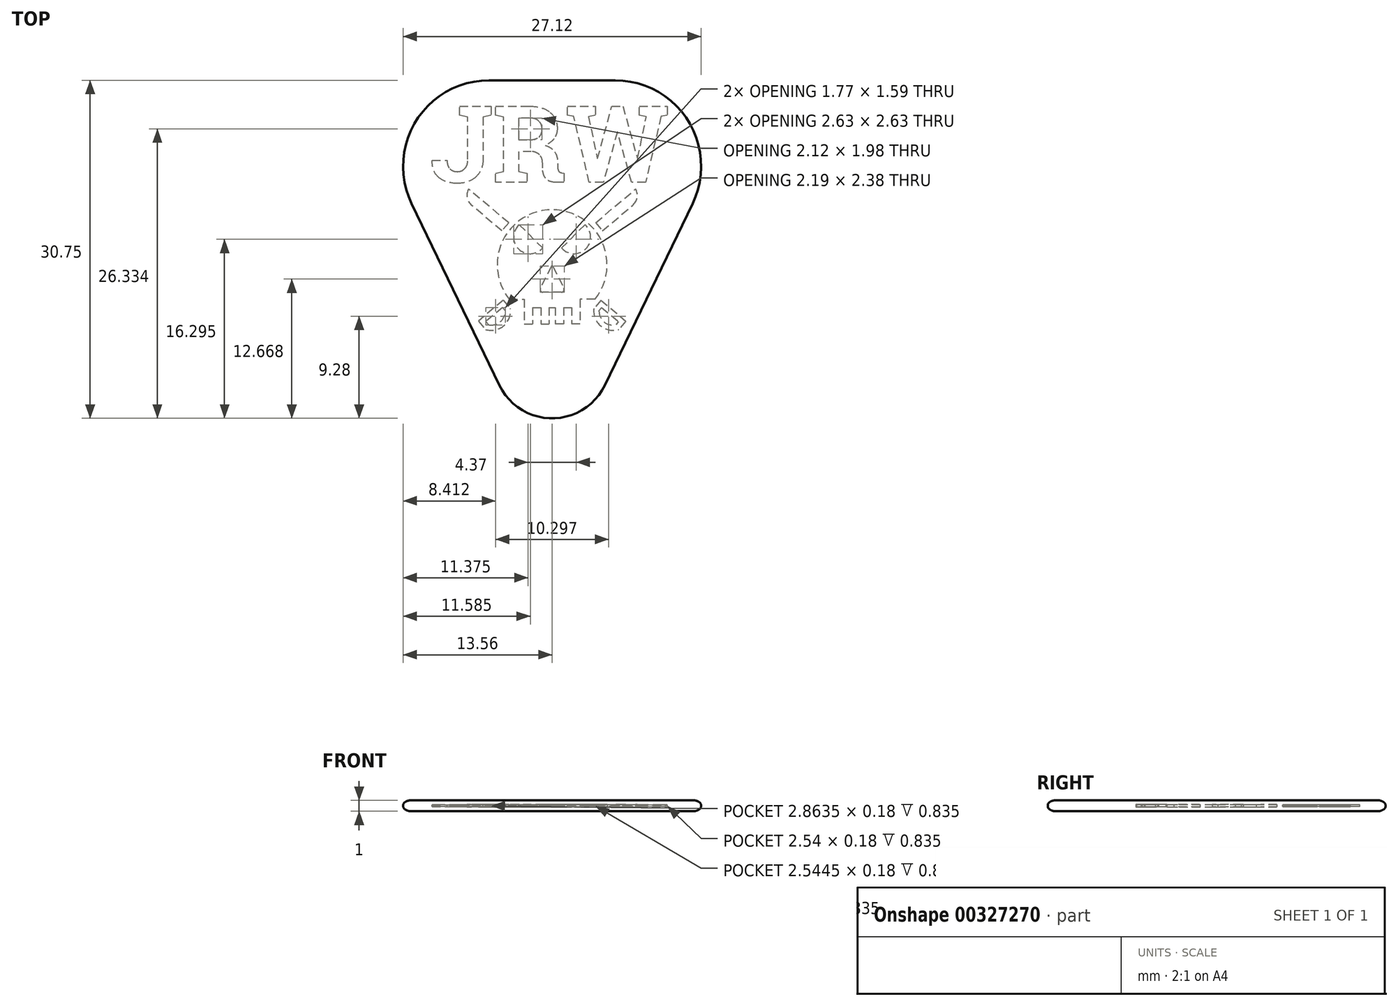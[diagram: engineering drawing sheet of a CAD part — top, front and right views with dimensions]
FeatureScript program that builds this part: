
annotation { "Feature Type Name" : "Feature", "Feature Type Description" : "" }
export const myFeature = defineFeature(function(context is Context, id is Id, definition is map)
    precondition{}
    {
        {
            var Q0;
            Q0=qCreatedBy(makeId("Top.planeOp"),FACE);
            var sketch = newSketch(context, id + "F0", { "sketchPlane" : qUnion([Q0])});
            skLineSegment(sketch, "E0", {"start": v(-5.74, 12.45) * mm, "end": v(5.74, 12.45) * mm});
            skLineSegment(sketch, "E1", {"start": v(12.95, 0.97) * mm, "end": v(4.95, -15.56) * mm});
            skLineSegment(sketch, "E2", {"start": v(-4.95, -15.56) * mm, "end": v(-12.95, 0.97) * mm});
            skPoint(sketch, "E3.visualSharp", {"position": v(-18.5, 12.45) * mm});
            skArc(sketch, "E3.filletArc", {"start": v(-5.74, 12.45) * mm, "mid": v(-12.52, 8.7) * mm, "end": v(-12.95, 0.97) * mm});
            skPoint(sketch, "E4.visualSharp", {"position": v(18.5, 12.45) * mm});
            skArc(sketch, "E4.filletArc", {"start": v(12.95, 0.97) * mm, "mid": v(12.52, 8.7) * mm, "end": v(5.74, 12.45) * mm});
            skPoint(sketch, "E5.visualSharp", {"position": v(0, -25.8) * mm});
            skArc(sketch, "E5.filletArc", {"start": v(-4.95, -15.56) * mm, "mid": v(0, -18.66) * mm, "end": v(4.95, -15.56) * mm});
            skSolve(sketch);
        }
        {
            var Q0;
            Q0=makeQuery(id+"F0.imprint","IMPRINT",FACE,{"disambiguationData":[TD([[makeQuery(id+"F0.imprint","IMPRINT",EDGE,{"derivedFrom":sQuery(id+"F0.wireOp",EDGE,"E0")}),-1.0]])]});
            extrude(context, id + "F1", {"entities" : qUnion([Q0]), "endBound" : BoundingType.SYMMETRIC, "depth" : 1 * mm, "offsetDistance" : 25 * mm});
        }
        {
            var Q0;
            Q0=makeQuery(id+"F1.opExtrude","CAP_EDGE",EDGE,{"disambiguationData":[OSD([sQuery(id+"F0.wireOp",EDGE,"E1")])],"isStart":false});
            var Q1;
            Q1=makeQuery(id+"F1.opExtrude","CAP_EDGE",EDGE,{"disambiguationData":[OSD([sQuery(id+"F0.wireOp",EDGE,"E1")])],"isStart":true});
            chamfer(context, id + "F2", {"entities" : qUnion([Q0, Q1]), "chamferType" : ChamferType.OFFSET_ANGLE, "width" : 0.5 * mm, "oppositeDirection" : false, "angle" : 45 * degree, "tangentPropagation" : true});
        }
        {
            var Q0;
            {var subQ0=sQuery(id+"F0.wireOp",EDGE,"E2");Q0=makeQuery(id+"F2.opChamfer","BLEND_EDGE",EDGE,{"blendedFrom":[makeQuery(id+"F1.opExtrude","CAP_EDGE",EDGE,{"disambiguationData":[OSD([subQ0])],"isStart":false}),makeQuery(id+"F1.opExtrude","CAP_FACE",FACE,{"disambiguationData":[OSD([sQuery(id+"F0.wireOp",EDGE,"E0"),sQuery(id+"F0.wireOp",EDGE,"E1"),subQ0,sQuery(id+"F0.wireOp",EDGE,"E3.filletArc"),sQuery(id+"F0.wireOp",EDGE,"E4.filletArc"),sQuery(id+"F0.wireOp",EDGE,"E5.filletArc")])],"isStart":false})],"blendedInto":[makeQuery(id+"F1.opExtrude","CAP_FACE",FACE,{"disambiguationData":[OSD([sQuery(id+"F0.wireOp",EDGE,"E0"),sQuery(id+"F0.wireOp",EDGE,"E1"),subQ0,sQuery(id+"F0.wireOp",EDGE,"E3.filletArc"),sQuery(id+"F0.wireOp",EDGE,"E4.filletArc"),sQuery(id+"F0.wireOp",EDGE,"E5.filletArc")])],"isStart":false})]});}
            var Q1;
            {var subQ0=sQuery(id+"F0.wireOp",EDGE,"E1");Q1=makeQuery(id+"F2.opChamfer","BLEND_EDGE",EDGE,{"blendedFrom":[makeQuery(id+"F1.opExtrude","CAP_EDGE",EDGE,{"disambiguationData":[OSD([subQ0])],"isStart":true}),makeQuery(id+"F1.opExtrude","CAP_FACE",FACE,{"disambiguationData":[OSD([sQuery(id+"F0.wireOp",EDGE,"E0"),subQ0,sQuery(id+"F0.wireOp",EDGE,"E2"),sQuery(id+"F0.wireOp",EDGE,"E3.filletArc"),sQuery(id+"F0.wireOp",EDGE,"E4.filletArc"),sQuery(id+"F0.wireOp",EDGE,"E5.filletArc")])],"isStart":true})],"blendedInto":[makeQuery(id+"F1.opExtrude","CAP_FACE",FACE,{"disambiguationData":[OSD([sQuery(id+"F0.wireOp",EDGE,"E0"),subQ0,sQuery(id+"F0.wireOp",EDGE,"E2"),sQuery(id+"F0.wireOp",EDGE,"E3.filletArc"),sQuery(id+"F0.wireOp",EDGE,"E4.filletArc"),sQuery(id+"F0.wireOp",EDGE,"E5.filletArc")])],"isStart":true})]});}
            fillet(context, id + "F3", {"entities" : qUnion([Q0, Q1]), "radius" : 1 * mm, "tangentPropagation" : true, "allowEdgeOverflow" : false});
        }
        {
            var Q0;
            Q0=qCreatedBy(makeId("Top.planeOp"),FACE);
            var sketch = newSketch(context, id + "F4", { "sketchPlane" : qUnion([Q0])});
            skText(sketch, "E6", { "text": "JRW", "fontName": "RobotoSlab-Bold.ttf"});
            const initialGuessF4  = {"E6": [-0.01108, 0.003, 1, 0, 0.007]};
            skSetInitialGuess(sketch, initialGuessF4);
            skSolve(sketch);
        }
        {
            var Q0;
            Q0=qSketchRegion(id+"F4",true);
            extrude(context, id + "F5", {"entities" : qUnion([Q0]), "operationType" : NewBodyOperationType.REMOVE, "endBound" : BoundingType.SYMMETRIC, "oppositeDirection" : true, "depth" : 0.18 * mm, "offsetDistance" : 25 * mm});
        }
        {
            var Q0;
            {var subQ0=sQuery(id+"F0.wireOp",EDGE,"E2");Q0=makeQuery(id+"F2.opChamfer","BLEND_EDGE",EDGE,{"blendedFrom":[makeQuery(id+"F1.opExtrude","CAP_EDGE",EDGE,{"disambiguationData":[OSD([subQ0])],"isStart":true}),makeQuery(id+"F1.opExtrude","CAP_EDGE",EDGE,{"disambiguationData":[OSD([subQ0])],"isStart":false})],"blendedInto":[]});}
            fillet(context, id + "F6", {"entities" : qUnion([Q0]), "radius" : 0.4 * mm, "tangentPropagation" : true, "allowEdgeOverflow" : false});
        }
        {
            var Q0;
            Q0=qCreatedBy(makeId("Top.planeOp"),FACE);
            var sketch = newSketch(context, id + "F7", { "sketchPlane" : qUnion([Q0])});
            skArc(sketch, "E7", {"start": v(3.9, -7.64) * mm, "mid": v(0, 0.5) * mm, "end": v(-3.9, -7.64) * mm});
            skLineSegment(sketch, "E8", {"start": v(-2.53, -8.81) * mm, "end": v(-2.53, -9.89) * mm});
            skLineSegment(sketch, "E9", {"start": v(-2.53, -9.89) * mm, "end": v(-1.78, -9.89) * mm});
            skLineSegment(sketch, "E10.MirrorCS", {"start": v(2.53, -9.89) * mm, "end": v(1.78, -9.89) * mm});
            skLineSegment(sketch, "E11.MirrorCS", {"start": v(2.53, -8.81) * mm, "end": v(2.53, -9.89) * mm});
            skLineSegment(sketch, "E12", {"start": v(-3.9, -7.64) * mm, "end": v(-2.53, -7.64) * mm});
            skLineSegment(sketch, "E13", {"start": v(-2.53, -7.64) * mm, "end": v(-2.53, -8.81) * mm});
            skLineSegment(sketch, "E14.MirrorCS", {"start": v(3.9, -7.64) * mm, "end": v(2.53, -7.64) * mm});
            skLineSegment(sketch, "E15.MirrorCS", {"start": v(2.53, -7.64) * mm, "end": v(2.53, -8.81) * mm});
            skArc(sketch, "E16", {"start": v(-2.99, -0.87) * mm, "mid": v(-3.06, -3.06) * mm, "end": v(-0.87, -2.99) * mm});
            skArc(sketch, "E17.MirrorC", {"start": v(2.99, -0.87) * mm, "mid": v(3.06, -3.06) * mm, "end": v(0.87, -2.99) * mm});
            skLineSegment(sketch, "E18", {"start": v(-1.78, -8.39) * mm, "end": v(-1.78, -9.89) * mm});
            skLineSegment(sketch, "E19", {"start": v(-1.03, -8.39) * mm, "end": v(-1.03, -9.89) * mm});
            skLineSegment(sketch, "E20.MirrorCS", {"start": v(1.78, -8.39) * mm, "end": v(1.78, -9.89) * mm});
            skLineSegment(sketch, "E21.MirrorCS", {"start": v(1.03, -8.39) * mm, "end": v(1.03, -9.89) * mm});
            skLineSegment(sketch, "E22", {"start": v(-0.28, -8.39) * mm, "end": v(-0.28, -9.89) * mm});
            skLineSegment(sketch, "E23.MirrorCS", {"start": v(0.28, -8.39) * mm, "end": v(0.28, -9.89) * mm});
            skLineSegment(sketch, "E24.trimOffspring", {"start": v(-1.03, -9.89) * mm, "end": v(-0.28, -9.89) * mm});
            skPoint(sketch, "E25.orphan", {"position": v(0, -9.89) * mm});
            skLineSegment(sketch, "E26.trimOffspring", {"start": v(1.03, -9.89) * mm, "end": v(0.28, -9.89) * mm});
            skLineSegment(sketch, "E27", {"start": v(-1.78, -8.39) * mm, "end": v(-1.03, -8.39) * mm});
            skLineSegment(sketch, "E28", {"start": v(-0.28, -8.39) * mm, "end": v(0.28, -8.39) * mm});
            skLineSegment(sketch, "E29", {"start": v(1.03, -8.39) * mm, "end": v(1.78, -8.39) * mm});
            skPoint(sketch, "E30.start.orphan", {"position": v(-1.78, -7.64) * mm});
            skPoint(sketch, "E31.orphan", {"position": v(-1.03, -7.64) * mm});
            skPoint(sketch, "E32.start.orphan", {"position": v(-0.28, -7.64) * mm});
            skPoint(sketch, "E33.orphan", {"position": v(0.28, -7.64) * mm});
            skPoint(sketch, "E34.start.orphan", {"position": v(1.03, -7.64) * mm});
            skPoint(sketch, "E35.orphan", {"position": v(1.78, -7.64) * mm});
            skLineSegment(sketch, "E36", {"start": v(-0.09, -4.68) * mm, "end": v(-1.07, -6.64) * mm});
            skLineSegment(sketch, "E37", {"start": v(-0.85, -7) * mm, "end": v(0, -7) * mm});
            skLineSegment(sketch, "E38.MirrorCS", {"start": v(0.09, -4.68) * mm, "end": v(1.07, -6.64) * mm});
            skLineSegment(sketch, "E39.MirrorCS", {"start": v(0.85, -7) * mm, "end": v(0, -7) * mm});
            skArc(sketch, "E40.filletArc", {"start": v(0.09, -4.68) * mm, "mid": v(0, -4.62) * mm, "end": v(-0.09, -4.68) * mm});
            skPoint(sketch, "E41.visualSharp", {"position": v(-1.25, -7) * mm});
            skArc(sketch, "E41.filletArc", {"start": v(-1.07, -6.64) * mm, "mid": v(-1.06, -6.88) * mm, "end": v(-0.85, -7) * mm});
            skPoint(sketch, "E42.visualSharp", {"position": v(1.25, -7) * mm});
            skArc(sketch, "E42.filletArc", {"start": v(0.85, -7) * mm, "mid": v(1.06, -6.88) * mm, "end": v(1.07, -6.64) * mm});
            skLineSegment(sketch, "E43", {"start": v(3.95, -0.68) * mm, "end": v(7.6, 2.38) * mm});
            skLineSegment(sketch, "E44", {"start": v(4.57, -1.42) * mm, "end": v(7.33, 0.9) * mm});
            skArc(sketch, "E45", {"start": v(7.33, 0.9) * mm, "mid": v(7.73, 1.59) * mm, "end": v(7.6, 2.38) * mm});
            skLineSegment(sketch, "E46", {"start": v(3.95, -0.68) * mm, "end": v(-3.79, -7.18) * mm, "construction": true});
            skLineSegment(sketch, "E47", {"start": v(-6.7, -9.63) * mm, "end": v(-6.06, -10.4) * mm});
            skLineSegment(sketch, "E48", {"start": v(3.95, -0.68) * mm, "end": v(4.57, -1.42) * mm});
            skLineSegment(sketch, "E49", {"start": v(-4.44, -7.73) * mm, "end": v(-3.8, -8.5) * mm});
            skLineSegment(sketch, "E50.trimOffspring", {"start": v(-4.44, -7.73) * mm, "end": v(-5.83, -8.9) * mm, "construction": true});
            skLineSegment(sketch, "E51.trimOffspring", {"start": v(-4.44, -7.73) * mm, "end": v(-6.7, -9.63) * mm});
            skPoint(sketch, "E52", {"position": v(-6.06, -10.4) * mm});
            skPoint(sketch, "E53.orphan", {"position": v(-5.42, -11.16) * mm});
            skArc(sketch, "E54", {"start": v(-6.06, -10.4) * mm, "mid": v(-4.41, -10.07) * mm, "end": v(-3.8, -8.5) * mm});
            skLineSegment(sketch, "E55.0", {"start": v(-4.5, -8.4) * mm, "end": v(-6.03, -9.69) * mm});
            skLineSegment(sketch, "E55.1", {"start": v(-4.5, -8.4) * mm, "end": v(-4.27, -8.69) * mm});
            skArc(sketch, "E55.2", {"start": v(-5.8, -9.97) * mm, "mid": v(-4.72, -9.7) * mm, "end": v(-4.27, -8.69) * mm});
            skLineSegment(sketch, "E55.3", {"start": v(-6.03, -9.69) * mm, "end": v(-5.8, -9.97) * mm});
            skLineSegment(sketch, "E56.MirrorCS", {"start": v(4.5, -8.4) * mm, "end": v(4.27, -8.69) * mm});
            skLineSegment(sketch, "E57.MirrorCS", {"start": v(6.03, -9.69) * mm, "end": v(5.8, -9.97) * mm});
            skLineSegment(sketch, "E58.MirrorCS", {"start": v(4.44, -7.73) * mm, "end": v(5.83, -8.9) * mm, "construction": true});
            skArc(sketch, "E59.MirrorCS", {"start": v(6.06, -10.4) * mm, "mid": v(4.41, -10.07) * mm, "end": v(3.8, -8.5) * mm});
            skLineSegment(sketch, "E60.MirrorCS", {"start": v(4.44, -7.73) * mm, "end": v(6.7, -9.63) * mm});
            skPoint(sketch, "E61.MirrorP", {"position": v(6.06, -10.4) * mm});
            skLineSegment(sketch, "E62.MirrorCS", {"start": v(4.5, -8.4) * mm, "end": v(6.03, -9.69) * mm});
            skLineSegment(sketch, "E63.MirrorCS", {"start": v(4.44, -7.73) * mm, "end": v(3.8, -8.5) * mm});
            skArc(sketch, "E64.MirrorCS", {"start": v(5.8, -9.97) * mm, "mid": v(4.72, -9.7) * mm, "end": v(4.27, -8.69) * mm});
            skPoint(sketch, "E65.MirrorP", {"position": v(5.42, -11.16) * mm});
            skLineSegment(sketch, "E66.MirrorCS", {"start": v(6.7, -9.63) * mm, "end": v(6.06, -10.4) * mm});
            skLineSegment(sketch, "E67.MirrorCS", {"start": v(-4.57, -1.42) * mm, "end": v(-7.33, 0.9) * mm});
            skArc(sketch, "E68.MirrorCS", {"start": v(-7.33, 0.9) * mm, "mid": v(-7.73, 1.59) * mm, "end": v(-7.6, 2.38) * mm});
            skLineSegment(sketch, "E69.MirrorCS", {"start": v(-3.95, -0.68) * mm, "end": v(-7.6, 2.38) * mm});
            skLineSegment(sketch, "E70.MirrorCS", {"start": v(-3.95, -0.68) * mm, "end": v(-4.57, -1.42) * mm});
            skPoint(sketch, "E71", {"position": v(0, -4) * mm});
            skLineSegment(sketch, "E72", {"start": v(-2.99, -0.87) * mm, "end": v(-0.87, -2.99) * mm});
            skLineSegment(sketch, "E73.MirrorCS", {"start": v(2.99, -0.87) * mm, "end": v(0.87, -2.99) * mm});
            skSolve(sketch);
        }
        {
            var Q0;
            Q0=qSketchRegion(id+"F7",true);
            var Q1;
            Q1=makeQuery(id+"F7.imprint","IMPRINT",FACE,{"disambiguationData":[TD([[makeQuery(id+"F7.imprint","IMPRINT",EDGE,{"derivedFrom":sQuery(id+"F7.wireOp",EDGE,"939ed108-b3df-4f31-88ce-246f36476dcc.0")}),-1.0]])]});
            var Q2;
            Q2=makeQuery(id+"F7.imprint","IMPRINT",FACE,{"disambiguationData":[TD([[makeQuery(id+"F7.imprint","IMPRINT",EDGE,{"derivedFrom":sQuery(id+"F7.wireOp",EDGE,"7208b4ee-4551-4fd0-8a5f-77d057b4d0f6.0")}),-1.0]])]});
            extrude(context, id + "F8", {"entities" : qUnion([Q0, Q1, Q2]), "operationType" : NewBodyOperationType.REMOVE, "endBound" : BoundingType.SYMMETRIC, "depth" : 0.2 * mm, "offsetDistance" : 25 * mm});
        }
    });
